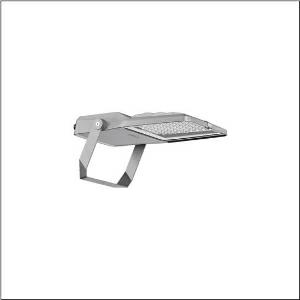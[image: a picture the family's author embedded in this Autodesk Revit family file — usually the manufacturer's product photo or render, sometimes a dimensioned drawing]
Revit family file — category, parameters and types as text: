
# Revit family: floodlight_fl_21_mini___pl43_5xa7776b4a1a_dd59
name_source: partatom
category: Lighting Fixtures
units: mm (PartAtom-declared; Revit-internal decimal feet)

## family parameters
Cut with Voids When Loaded = No
Host = Face
Light Source = No
Part Type = Normal
Room Calculation Point = No
Round Connector Dimension = Use Diameter
Shared = No

## types (1)
- --- (1 x LED, 6650 lm, 45.7 W, 4000K)
    Apparent Load = 46 VA
    CIE Flux Codes = 27 78 99 100 100
    Color Rendering = 70
    Color Temperature = 4000K
    Default Elevation = 1800 mm
    Description = Floodlight FL 21 mini, floodlight, primary light control with lens, of PMMA, primary optical cover: protective disc, of toughened safety glass, transparent, light distribution: PL43, light emission: direct distribution, installation type: surface-mounted, LED, High Power LED, rated luminous flux: 6.650lm, luminous efficacy: 146lm/W, light colour: 740, colour temperature: 4000K, control gear: D4iSmart Interface (Zhaga), control: overheat protection, constant luminous flux control, time-dependent luminous flux control, flexible luminous flux parameterisation, pre-setting: logarithmic dimming characteristic, with terminal, 6-pole, mains connection: 220..240V, AC, 50/60Hz, start of lifetime: 46W, end of service life: 48W, reduction: 22W, mounting bracket, of diecast aluminium, powder-coated, Siteco® metallic grey (DB 702S), corrosivity category C5 mid according to DIN EN ISO 12944, suitable for swimming pools, chlorine-resistant, sealing non-destructively replaceable, mounting bracket, of steel, galvanised, powder-coated, Siteco® metallic grey (DB 702S), Smart Interface below and above, protection rating (complete): IP66, insulation class (complete): insulation class II (safety insulation), certification: CE, ENEC, VDE, protection symbol: D, impact resistance: IK08, permissible operating ambient temperature: -40..+40°C, permissible operating ambient temperature for outdoor applications: -40..+50°C, standard: DIN EN 12944, LABS conformity tested according to VDMA 24364:2018-05, packaging unit: 1 piece

Light Distribution: PL43
    Height = 70 mm
    Lamp = 1 x LED
    Lamp Light Flux = 6650 lm
    Lamp Power = 45.7 W
    Lamp count = 1
    Length = 485 mm
    Luminous efficacy = 146 lm/W
    Manufacturer = Siteco
    ModVariant = No
    Model = 5XA7776B4A1A
    Number of Poles = 1
    OnlyDefault = Yes
    Power Factor = 1
    Product Name = Floodlight FL 21 mini | PL43
    Product group = floodlight | pylon annexe
    ProductGroupID = 6200
    Protection Class = Protection class II
    Protection Degree = IP 66
    RLX_Detail_Level = 1
    RLX_Emergency_Light_Flux = 0 lm
    RLX_Emergency_Type = 0
    RLX_Emergency_Type_DB = No
    RlxData = <blob elided: 95933 chars, md5=46110674>
    Socket = socket
    Standby Power = 0 W
    System Light Flux = 6650 lm
    System Power = 46 W
    Type Comments = factory setting: luminous flux: 100 % | dim-lin: 254 | 463 mA
    Type Image = l_1006845.jpg
    URL = http://relux.com
    VarID = @adj_095302
    Voltage = 0 V
    Weight = 0.00 kg
    Width = 337 mm

## geometry (parser evidence)
native form markers: Blend x4, Sweep x12
no freeform markers — native parametric forms only
